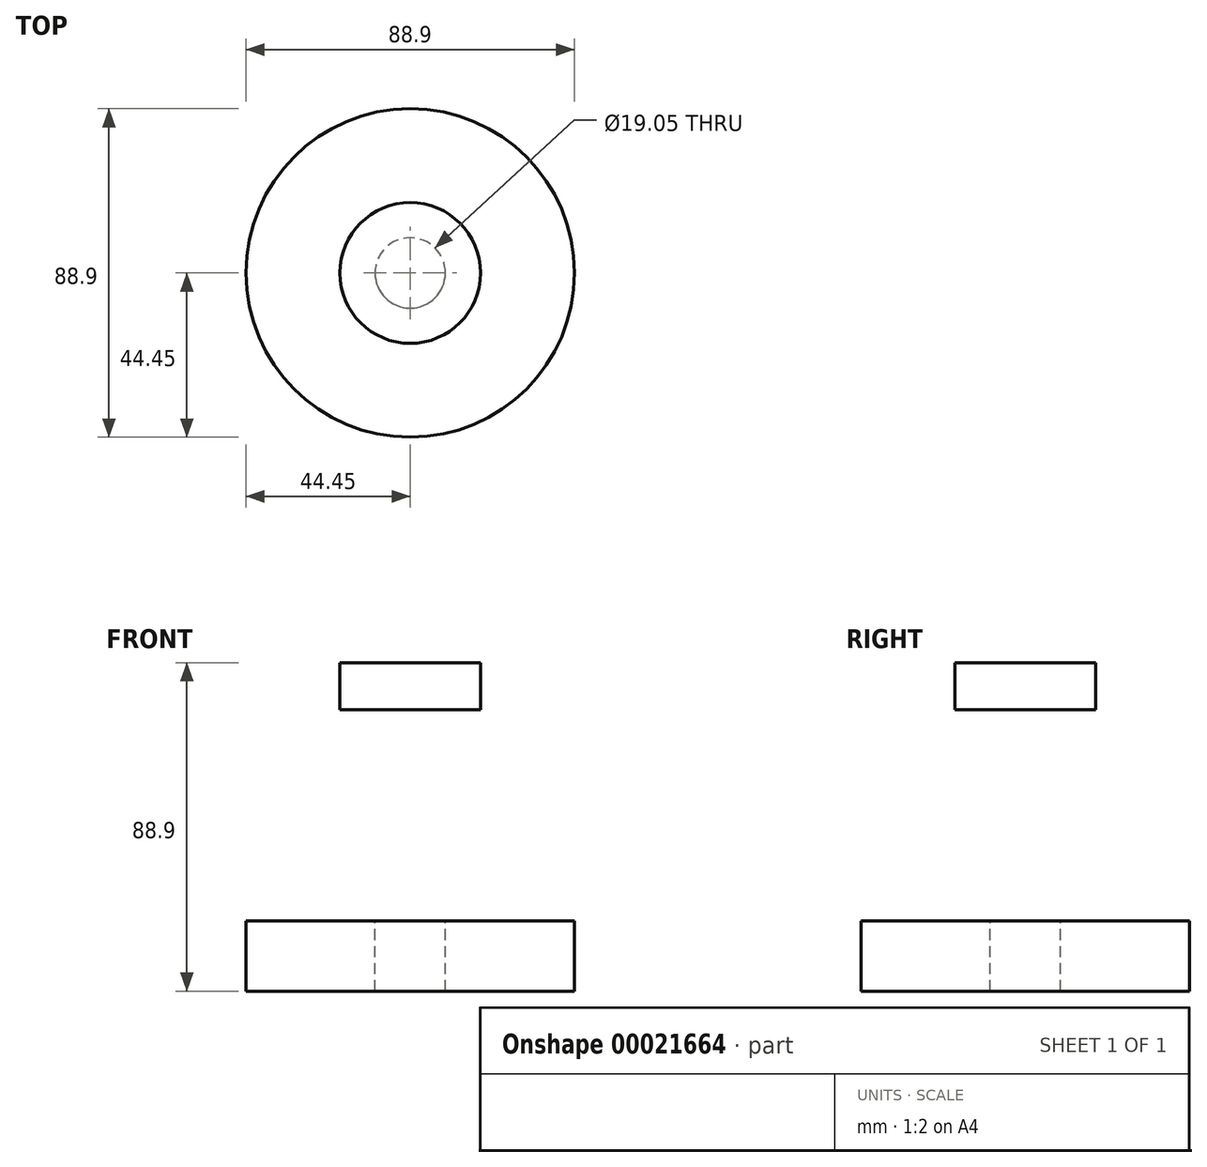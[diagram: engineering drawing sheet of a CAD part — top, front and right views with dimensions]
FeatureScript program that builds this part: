
annotation { "Feature Type Name" : "Feature", "Feature Type Description" : "" }
export const myFeature = defineFeature(function(context is Context, id is Id, definition is map)
    precondition{}
    {
        {
            var Q0;
            Q0=qCreatedBy(makeId("Front.planeOp"),FACE);
            var sketch = newSketch(context, id + "F0", { "sketchPlane" : qUnion([Q0])});
            skLineSegment(sketch, "E0", {"start": v(0, 52.84) * mm, "end": v(0, -76.2) * mm});
            skLineSegment(sketch, "E1", {"start": v(0, -76.2) * mm, "end": v(44.45, -76.2) * mm});
            skLineSegment(sketch, "E2", {"start": v(44.45, -76.2) * mm, "end": v(44.45, -57.15) * mm});
            skLineSegment(sketch, "E3", {"start": v(44.45, -57.15) * mm, "end": v(25.4, -57.15) * mm});
            skLineSegment(sketch, "E4", {"start": v(25.4, -57.15) * mm, "end": v(0, -57.15) * mm});
            skLineSegment(sketch, "E5", {"start": v(0, -57.15) * mm, "end": v(25.4, -57.15) * mm});
            skLineSegment(sketch, "E6", {"start": v(25.4, -57.15) * mm, "end": v(25.4, 0) * mm});
            skLineSegment(sketch, "E7", {"start": v(19.05, 0) * mm, "end": v(19.05, 12.7) * mm});
            skLineSegment(sketch, "E8", {"start": v(19.05, 12.7) * mm, "end": v(0, 12.7) * mm});
            skLineSegment(sketch, "E9", {"start": v(0, 0) * mm, "end": v(19.05, 0) * mm});
            skLineSegment(sketch, "E10", {"start": v(25.4, 0) * mm, "end": v(19.05, 0) * mm});
            skPoint(sketch, "E11", {"position": v(0, 52.84) * mm});
            skSolve(sketch);
        }
        {
            var Q0;
            {var subQ1=sQuery(id+"F0.wireOp",EDGE,"E5");Q0=makeQuery(id+"F0.imprint","IMPRINT",FACE,{"disambiguationData":[TD([[makeQuery(id+"F0.imprint","IMPRINT",EDGE,{"derivedFrom":subQ1}),1.0]])]});}
            var Q1;
            Q1=makeQuery(id+"F0.imprint","IMPRINT",FACE,{"disambiguationData":[TD([[makeQuery(id+"F0.imprint","IMPRINT",EDGE,{"derivedFrom":sQuery(id+"F0.wireOp",EDGE,"E7")}),1.0]])]});
            var Q2;
            {var subQ1=sQuery(id+"F0.wireOp",EDGE,"E1");Q2=makeQuery(id+"F0.imprint","IMPRINT",FACE,{"disambiguationData":[TD([[makeQuery(id+"F0.imprint","IMPRINT",EDGE,{"derivedFrom":subQ1}),1.0]])]});}
            var Q3;
            Q3=sQuery(id+"F0.wireOp",EDGE,"E0");
            revolve(context, id + "F1", {"entities" : qUnion([Q0, Q1, Q2]), "axis" : qUnion([Q3]), "revolveType" : RevolveType.FULL});
        }
        {
            var Q0;
            Q0=qCreatedBy(makeId("Top.planeOp"),FACE);
            var sketch = newSketch(context, id + "F2", { "sketchPlane" : qUnion([Q0])});
            skPoint(sketch, "E12", {"position": v(0, 0) * mm});
            skLineSegment(sketch, "E13", {"start": v(-19.23, 0) * mm, "end": v(0, 0) * mm});
            skLineSegment(sketch, "E14", {"start": v(19.23, 0) * mm, "end": v(0, 0) * mm});
            skSolve(sketch);
        }
        {
            var Q0;
            Q0=sQuery(id+"F2.wireOp",VERTEX,"E12");
            var Q1;
            Q1=makeQuery(id+"F1.opRevolve","SWEPT_BODY",BODY,{"disambiguationData":[OSD([sQuery(id+"F0.wireOp",EDGE,"E0"),sQuery(id+"F0.wireOp",EDGE,"E1"),sQuery(id+"F0.wireOp",EDGE,"E2"),sQuery(id+"F0.wireOp",EDGE,"E3"),sQuery(id+"F0.wireOp",EDGE,"E6"),sQuery(id+"F0.wireOp",EDGE,"E7"),sQuery(id+"F0.wireOp",EDGE,"E8"),sQuery(id+"F0.wireOp",EDGE,"E10")])]});
            hole(context, id + "F3", {"style" : HoleStyle.SIMPLE, "holeDiameter" : 19.05 * mm, "endStyle" : HoleEndStyle.BLIND, "holeDepth" : 127 * mm, "locations" : qUnion([Q0]), "scope" : qUnion([Q1])});
        }
        {
            var Q0;
            Q0=sQuery(id+"F2.wireOp",VERTEX,"E12");
            var Q1;
            Q1=makeQuery(id+"F1.opRevolve","SWEPT_BODY",BODY,{"disambiguationData":[OSD([sQuery(id+"F0.wireOp",EDGE,"E0"),sQuery(id+"F0.wireOp",EDGE,"E1"),sQuery(id+"F0.wireOp",EDGE,"E2"),sQuery(id+"F0.wireOp",EDGE,"E3"),sQuery(id+"F0.wireOp",EDGE,"E6"),sQuery(id+"F0.wireOp",EDGE,"E7"),sQuery(id+"F0.wireOp",EDGE,"E8"),sQuery(id+"F0.wireOp",EDGE,"E10")])]});
            hole(context, id + "F4", {"style" : HoleStyle.SIMPLE, "holeDiameter" : 19.05 * mm, "endStyle" : HoleEndStyle.THROUGH, "oppositeDirection" : true, "locations" : qUnion([Q0]), "scope" : qUnion([Q1])});
        }
    });
